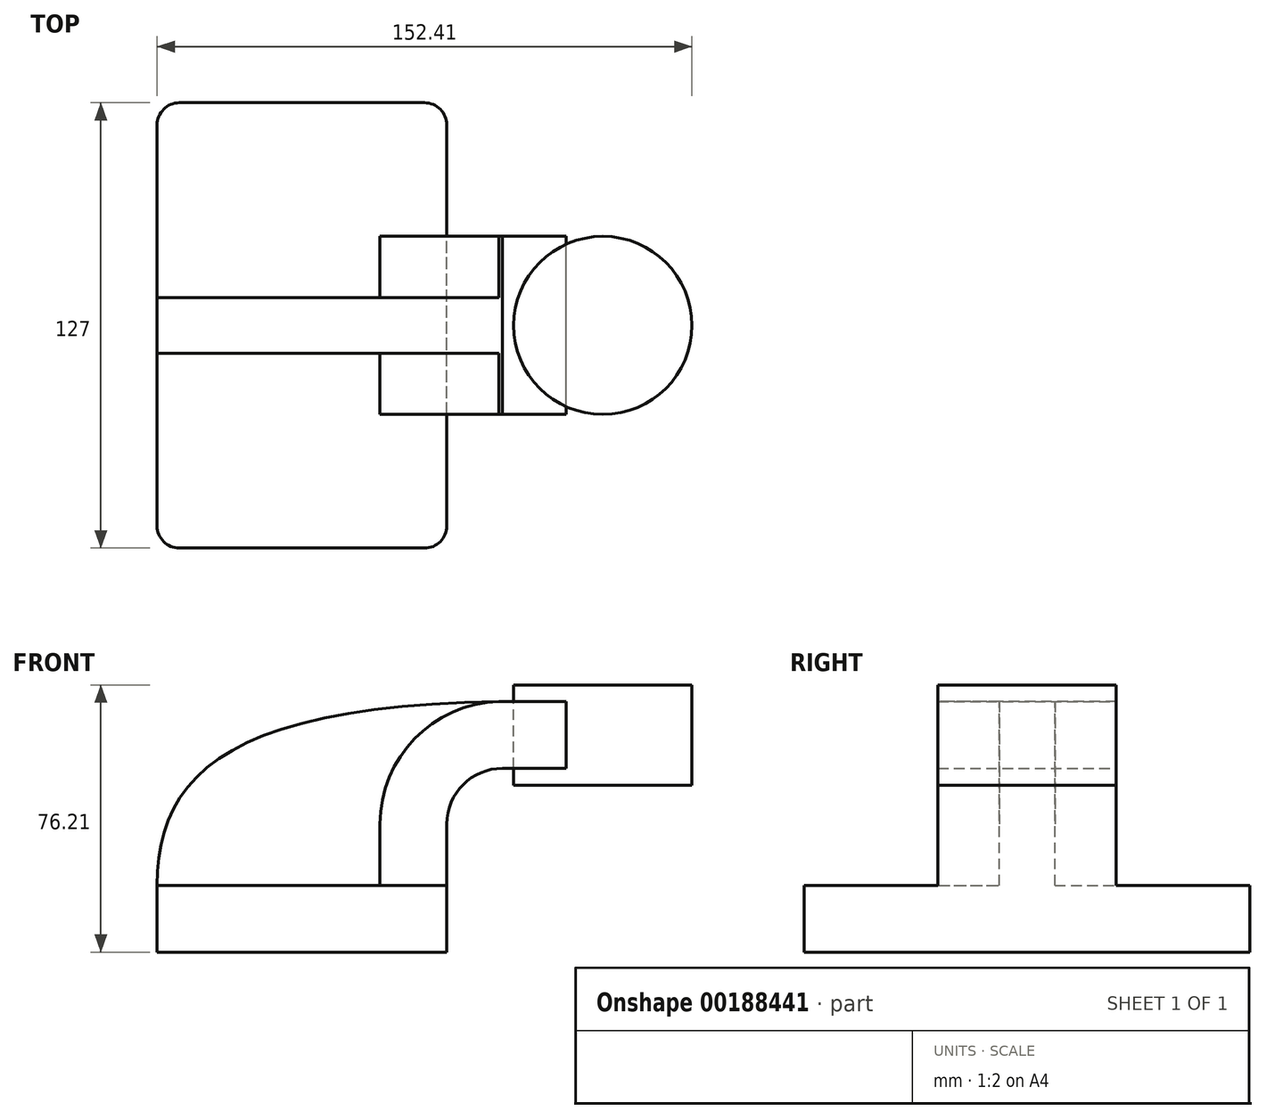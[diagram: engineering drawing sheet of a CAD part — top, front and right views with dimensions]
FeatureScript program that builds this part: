
annotation { "Feature Type Name" : "Feature", "Feature Type Description" : "" }
export const myFeature = defineFeature(function(context is Context, id is Id, definition is map)
    precondition{}
    {
        {
            var Q0;
            Q0=qCreatedBy(makeId("Front.planeOp"),FACE);
            var sketch = newSketch(context, id + "F0", { "sketchPlane" : qUnion([Q0])});
            skLineSegment(sketch, "E0.bottom", {"start": v(-41.28, 9.52) * mm, "end": v(41.28, 9.53) * mm});
            skLineSegment(sketch, "E0.top", {"start": v(-41.28, -9.53) * mm, "end": v(41.28, -9.53) * mm});
            skLineSegment(sketch, "E0.left", {"start": v(-41.28, 9.52) * mm, "end": v(-41.28, -9.53) * mm});
            skLineSegment(sketch, "E0.right", {"start": v(41.28, 9.53) * mm, "end": v(41.28, -9.52) * mm});
            skPoint(sketch, "E0.middle", {"position": v(0, 0) * mm});
            skLineSegment(sketch, "E1.bottom", {"start": v(111.12, 38.1) * mm, "end": v(60.32, 38.1) * mm});
            skLineSegment(sketch, "E1.top", {"start": v(111.12, 66.67) * mm, "end": v(60.32, 66.67) * mm});
            skLineSegment(sketch, "E1.left", {"start": v(111.12, 38.1) * mm, "end": v(111.12, 66.68) * mm});
            skLineSegment(sketch, "E1.right", {"start": v(60.32, 38.1) * mm, "end": v(60.32, 66.67) * mm});
            skPoint(sketch, "E1.middle", {"position": v(85.72, 52.39) * mm});
            skLineSegment(sketch, "E2", {"start": v(41.27, 9.53) * mm, "end": v(41.27, 27) * mm});
            skArc(sketch, "E3", {"start": v(41.27, 27) * mm, "mid": v(45.92, 38.23) * mm, "end": v(57.15, 42.88) * mm});
            skLineSegment(sketch, "E4", {"start": v(57.15, 42.88) * mm, "end": v(75.33, 42.88) * mm});
            skLineSegment(sketch, "E5.0", {"start": v(57.15, 61.93) * mm, "end": v(75.33, 61.93) * mm});
            skArc(sketch, "E5.1", {"start": v(22.22, 27) * mm, "mid": v(32.45, 51.7) * mm, "end": v(57.15, 61.93) * mm});
            skLineSegment(sketch, "E5.2", {"start": v(22.22, 9.53) * mm, "end": v(22.22, 27) * mm});
            skLineSegment(sketch, "E6", {"start": v(75.33, 42.88) * mm, "end": v(75.33, 61.93) * mm});
            skFitSpline(sketch, "E7", {"points": [v(-41.28, 9.53) * mm, v(57.15, 61.93) * mm], "startDerivative": vector(-0.03, 93) * mm, "endDerivative": vector(236.78, 3.2) * mm});
            skLineSegment(sketch, "E8", {"start": v(85.72, 52.39) * mm, "end": v(85.72, 66.67) * mm});
            skLineSegment(sketch, "E9", {"start": v(85.72, 66.67) * mm, "end": v(85.72, 38.1) * mm});
            skLineSegment(sketch, "E10", {"start": v(83.3, 66.67) * mm, "end": v(83.3, 38.1) * mm});
            skSolve(sketch);
        }
        {
            var Q0;
            Q0=makeQuery(id+"F0.imprint","IMPRINT",FACE,{"disambiguationData":[TD([[makeQuery(id+"F0.imprint","IMPRINT",EDGE,{"derivedFrom":sQuery(id+"F0.wireOp",EDGE,"E0.top")}),1.0]])]});
            extrude(context, id + "F1", {"entities" : qUnion([Q0]), "endBound" : BoundingType.SYMMETRIC, "depth" : 127 * mm});
        }
        {
            var Q0;
            {var subQ1=sQuery(id+"F0.wireOp",EDGE,"E2");Q0=makeQuery(id+"F0.imprint","IMPRINT",FACE,{"disambiguationData":[TD([[makeQuery(id+"F0.imprint","IMPRINT",EDGE,{"derivedFrom":subQ1}),1.0]])]});}
            var Q1;
            {var subQ5=sQuery(id+"F0.wireOp",EDGE,"E6");Q1=makeQuery(id+"F0.imprint","IMPRINT",FACE,{"disambiguationData":[TD([[makeQuery(id+"F0.imprint","IMPRINT",EDGE,{"derivedFrom":subQ5}),1.0]])]});}
            extrude(context, id + "F2", {"entities" : qUnion([Q0, Q1]), "operationType" : NewBodyOperationType.ADD, "endBound" : BoundingType.SYMMETRIC, "depth" : 50.8 * mm});
        }
        {
            var Q0;
            {var subQ3=sQuery(id+"F0.wireOp",EDGE,"E5.2");Q0=makeQuery(id+"F0.imprint","IMPRINT",FACE,{"disambiguationData":[TD([[makeQuery(id+"F0.imprint","IMPRINT",EDGE,{"derivedFrom":subQ3}),1.0]])]});}
            extrude(context, id + "F3", {"entities" : qUnion([Q0]), "operationType" : NewBodyOperationType.ADD, "endBound" : BoundingType.SYMMETRIC, "depth" : 15.88 * mm});
        }
        {
            var Q0;
            Q0=makeQuery(id+"F1.opExtrude","CAP_EDGE",EDGE,{"disambiguationData":[OSD([sQuery(id+"F0.wireOp",EDGE,"E0.right")])],"isStart":false});
            var Q1;
            Q1=makeQuery(id+"F1.opExtrude","CAP_EDGE",EDGE,{"disambiguationData":[OSD([sQuery(id+"F0.wireOp",EDGE,"E0.left")])],"isStart":false});
            var Q2;
            Q2=makeQuery(id+"F1.opExtrude","CAP_EDGE",EDGE,{"disambiguationData":[OSD([sQuery(id+"F0.wireOp",EDGE,"E0.right")])],"isStart":true});
            var Q3;
            Q3=makeQuery(id+"F1.opExtrude","CAP_EDGE",EDGE,{"disambiguationData":[OSD([sQuery(id+"F0.wireOp",EDGE,"E0.left")])],"isStart":true});
            fillet(context, id + "F4", {"entities" : qUnion([Q0, Q1, Q2, Q3]), "radius" : 6.35 * mm, "tangentPropagation" : true, "allowEdgeOverflow" : false});
        }
        {
            var Q0;
            {var subQ4=sQuery(id+"F0.wireOp",EDGE,"E1.left");Q0=makeQuery(id+"F0.imprint","IMPRINT",FACE,{"disambiguationData":[TD([[makeQuery(id+"F0.imprint","IMPRINT",EDGE,{"derivedFrom":subQ4}),1.0]])]});}
            var Q1;
            Q1=sQuery(id+"F0.wireOp",EDGE,"E9");
            revolve(context, id + "F5", {"entities" : qUnion([Q0]), "axis" : qUnion([Q1]), "revolveType" : RevolveType.FULL});
        }
    });
